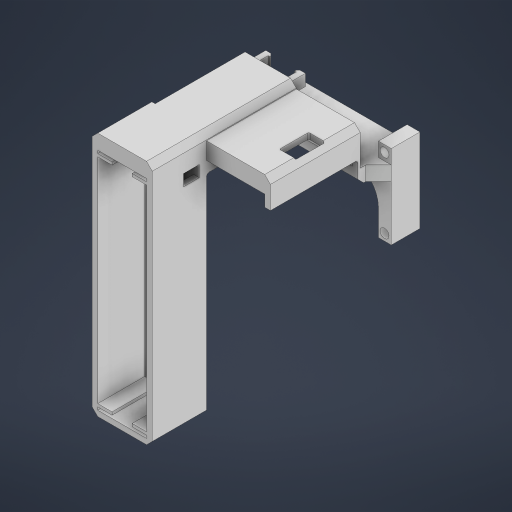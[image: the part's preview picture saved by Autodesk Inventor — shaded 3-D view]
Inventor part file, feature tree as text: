
AUTODESK INVENTOR PART (.ipt)
format: ipt  version: 2024.1 (Build 281209000, 209)  size: 566,272 bytes
history: native  units: in
note: dims shown in document units (in); Inventor stores cm internally (conversion verified against a paired STEP export)
features: reference x18, extrude x16, sketch x11, projected_geometry x10, other x9, chamfer x4, fillet x2, plane x1
ambient origin geometry x8: Origin, YZ Plane, XZ Plane, XY Plane, X Axis, Y Axis, Z Axis, Center Point
bodies: Solid1 (feature_tree)
feature tree (71):
  sketch  "Sketch1"  dims[d0=0.002in d1=0.1254in]
  extrude  "Extrusion1"  Depth=0.1254in
  extrude  "Extrusion2"  Depth=0.25in TaperAngle=0.0deg
  plane  "Work Plane1"
  sketch  "Sketch2"  dims[d2=0.015in d3=0.25in d4=0.0in]
  extrude  "Extrusion3"  Depth=0.429in
  extrude  "Extrusion4"  Depth=0.005in
  extrude  "Extrusion5"  Depth=0.0625in
  extrude  "Extrusion6"  Depth=0.15in
  extrude  "Extrusion7"  Depth=0.0625in TaperAngle=0.0deg
  extrude  "Extrusion8"  Depth=0.05in TaperAngle=0.0deg
  sketch  "Sketch5"  dims[d10=0.002in d11=0.0625in]
  extrude  "Extrusion9"  Depth=0.025in
  extrude  "Extrusion10"  Depth=0.175in
  extrude  "Extrusion11"  Depth=0.025in
  extrude  "Extrusion12"  Depth=0.175in
  chamfer  "Chamfer1"  Distance=0.0125in
  fillet  "Fillet2"  Radius=0.1in
  chamfer  "Chamfer2"  Distance=0.05in
  extrude  "Extrusion13"  Depth=0.05in
  fillet  "Fillet3"  Radius=0.05in
  extrude  "Extrusion14"  Depth=0.125in TaperAngle=0.0deg
  chamfer  "Chamfer3"  Distance=0.05in
  extrude  "Extrusion15"  TaperAngle=0.0deg  [1 undecoded]
  extrude  "Extrusion16"  Depth=0.2in
  chamfer  "Chamfer4"  Distance=0.1in
  reference  "Reference1"
  reference  "Reference2"
  reference  "Reference3"
  reference  "Reference4"
  reference  "Reference5"
  reference  "Reference6"
  projected_geometry  "Projected Loop1"
  reference  "Reference7"
  reference  "Reference8"
  reference  "Reference9"
  reference  "Reference10"
  reference  "Reference11"
  reference  "Reference12"
  sketch  "Sketch3"  dims[d5=0.429in d6=0.0in d7=0.002in]
  projected_geometry  "Projected Loop2"
  sketch  "Sketch4"  dims[d8=0.0in d9=0.005in]
  projected_geometry  "Projected Loop3"
  projected_geometry  "Projected Loop4"
  reference  "Reference13"
  sketch  "Sketch6"  dims[d12=0.067in d13=0.15in]
  projected_geometry  "Projected Loop5"
  sketch  "Sketch7"  dims[d14=0.0625in d15=0.0in d16=0.459in d17=0.0in]
  reference  "Reference14"
  reference  "Reference15"
  projected_geometry  "Projected Loop6"
  sketch  "Sketch8"  dims[d18=0.488in d19=0.0in d20=0.05in d21=0.0in]
  projected_geometry  "Projected Loop7"
  projected_geometry  "Projected Loop8"
  sketch  "Sketch9"  dims[d22=0.0125in d23=0.0in d24=0.025in]
  reference  "Reference16"
  reference  "Reference17"
  sketch  "Sketch10"  dims[d25=0.025in d26=0.175in]
  reference  "Reference18"
  sketch  "Sketch11"  dims[d27=0.025in d28=0.025in d29=0.175in d30=0.0125in d31=0.0in d32=0.1in d33=0.05in d35=0.05in d36=0.05in d37=1.0in d38=0.0in d39=0.05in d40=0.0in d41=0.0in d42=0.0in d43=0.2in d44=0.1in d45=0.0in d47=0.05in d48=0.125in d49=45.0deg d50=0.25in d51=0.112in d52=0.125in d53=45.0deg d54=0.1388in d55=0.0in d56=0.025in d57=0.35in d58=0.0in d59=0.01in d60=0.125in d61=45.0deg d62=0.005in d63=0.05in d64=0.1in d65=0.05in d66=0.1in d67=0.14in d68=0.0in d69=0.015in d70=0.015in d71=0.03in d72=0.0in d73=0.02in d74=0.125in d75=45.0deg]
  projected_geometry  "Projected Loop9"
  projected_geometry  "Projected Loop10"
  other  "<userpath>\Documents\School\FallCAD\Bio\Bio.iam"
  other  "Bio.iam"
  other  "arduino nano:1"
  other  "Servo HS425BB:1"
  other  "CUI_DEVICES_TS04-66-50-BK-160-SMT:1"
  other  "CUI_DEVICES_TS04-66-50-BK-160-SMT_2:1"
  other  "AAA Battery:1"
  other  "CUI_DEVICES_TS04-66-50-BK-160-SMT_1:1"
  other  "Leg_MIR:1"
note: 1 required parameter value undecoded (feature->parameter linkage not recoverable at this tier; creation-order binding heuristic only, values carry confidence <= 0.55)
